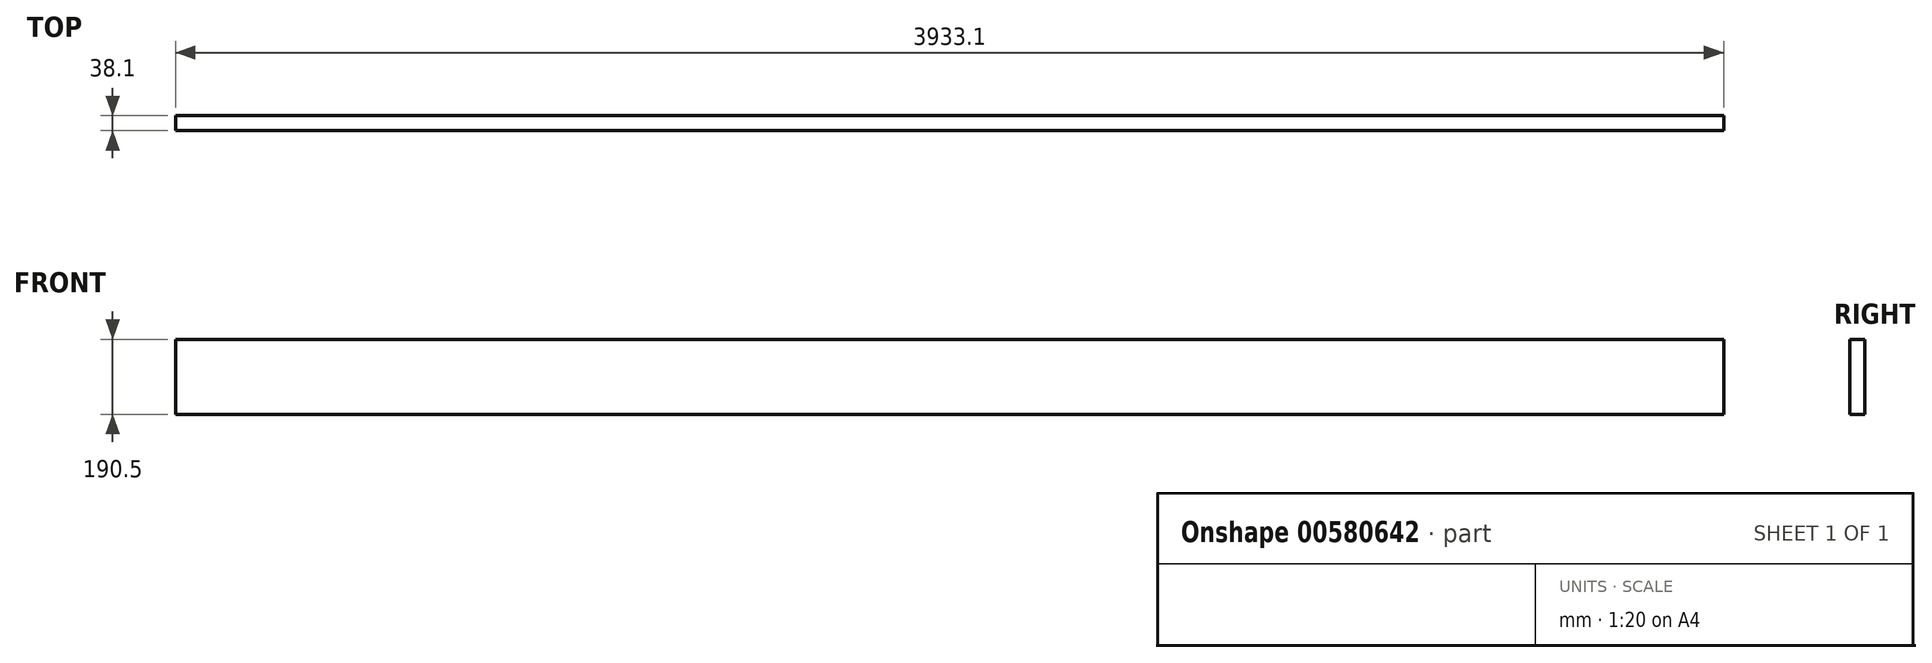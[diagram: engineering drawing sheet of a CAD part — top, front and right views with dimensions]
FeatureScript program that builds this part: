
annotation { "Feature Type Name" : "Feature", "Feature Type Description" : "" }
export const myFeature = defineFeature(function(context is Context, id is Id, definition is map)
    precondition{}
    {
        {
            var Q0;
            Q0=qCreatedBy(makeId("Top.planeOp"),FACE);
            var sketch = newSketch(context, id + "F0", { "sketchPlane" : qUnion([Q0])});
            skLineSegment(sketch, "E0.bottom", {"start": v(1966.55, -19.05) * mm, "end": v(-1966.55, -19.05) * mm});
            skLineSegment(sketch, "E0.top", {"start": v(1966.55, 19.05) * mm, "end": v(-1966.55, 19.05) * mm});
            skLineSegment(sketch, "E0.left", {"start": v(1966.55, -19.05) * mm, "end": v(1966.55, 19.05) * mm});
            skLineSegment(sketch, "E0.right", {"start": v(-1966.55, -19.05) * mm, "end": v(-1966.55, 19.05) * mm});
            skPoint(sketch, "E0.middle", {"position": v(0, 0) * mm});
            skSolve(sketch);
        }
        {
            var Q0;
            Q0=makeQuery(id+"F0.imprint","IMPRINT",FACE,{"disambiguationData":[TD([[makeQuery(id+"F0.imprint","IMPRINT",EDGE,{"derivedFrom":sQuery(id+"F0.wireOp",EDGE,"E0.bottom")}),-1.0]])]});
            extrude(context, id + "F1", {"entities" : qUnion([Q0]), "depth" : 190.5 * mm, "offsetDistance" : 25.4 * mm});
        }
    });
